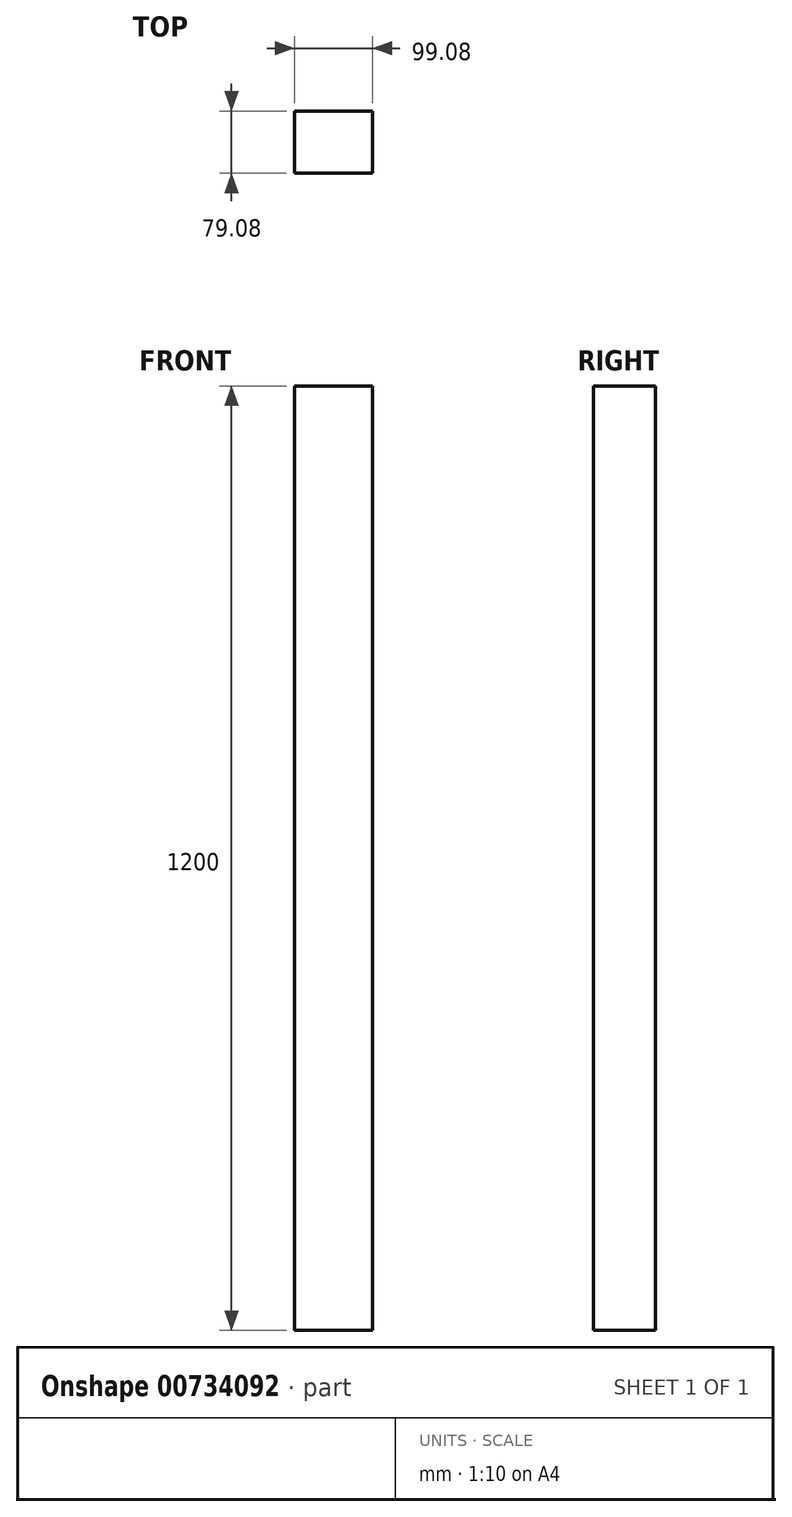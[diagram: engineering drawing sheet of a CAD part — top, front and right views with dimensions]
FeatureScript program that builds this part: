
annotation { "Feature Type Name" : "Feature", "Feature Type Description" : "" }
export const myFeature = defineFeature(function(context is Context, id is Id, definition is map)
    precondition{}
    {
        {
            var Q0;
            Q0=qCreatedBy(makeId("Top.planeOp"),FACE);
            var sketch = newSketch(context, id + "F0", { "sketchPlane" : qUnion([Q0])});
            skLineSegment(sketch, "E0.bottom", {"start": v(49.54, -39.54) * mm, "end": v(-49.54, -39.54) * mm});
            skLineSegment(sketch, "E0.top", {"start": v(49.54, 39.54) * mm, "end": v(-49.54, 39.54) * mm});
            skLineSegment(sketch, "E0.left", {"start": v(49.54, -39.54) * mm, "end": v(49.54, 39.54) * mm});
            skLineSegment(sketch, "E0.right", {"start": v(-49.54, -39.54) * mm, "end": v(-49.54, 39.54) * mm});
            skPoint(sketch, "E0.middle", {"position": v(0, 0) * mm});
            skSolve(sketch);
        }
        {
            var Q0;
            Q0=makeQuery(id+"F0.imprint","IMPRINT",FACE,{"disambiguationData":[TD([[makeQuery(id+"F0.imprint","IMPRINT",EDGE,{"derivedFrom":sQuery(id+"F0.wireOp",EDGE,"E0.bottom")}),-1.0]])]});
            extrude(context, id + "F1", {"entities" : qUnion([Q0]), "depth" : 1200 * mm, "offsetDistance" : 25 * mm});
        }
    });
